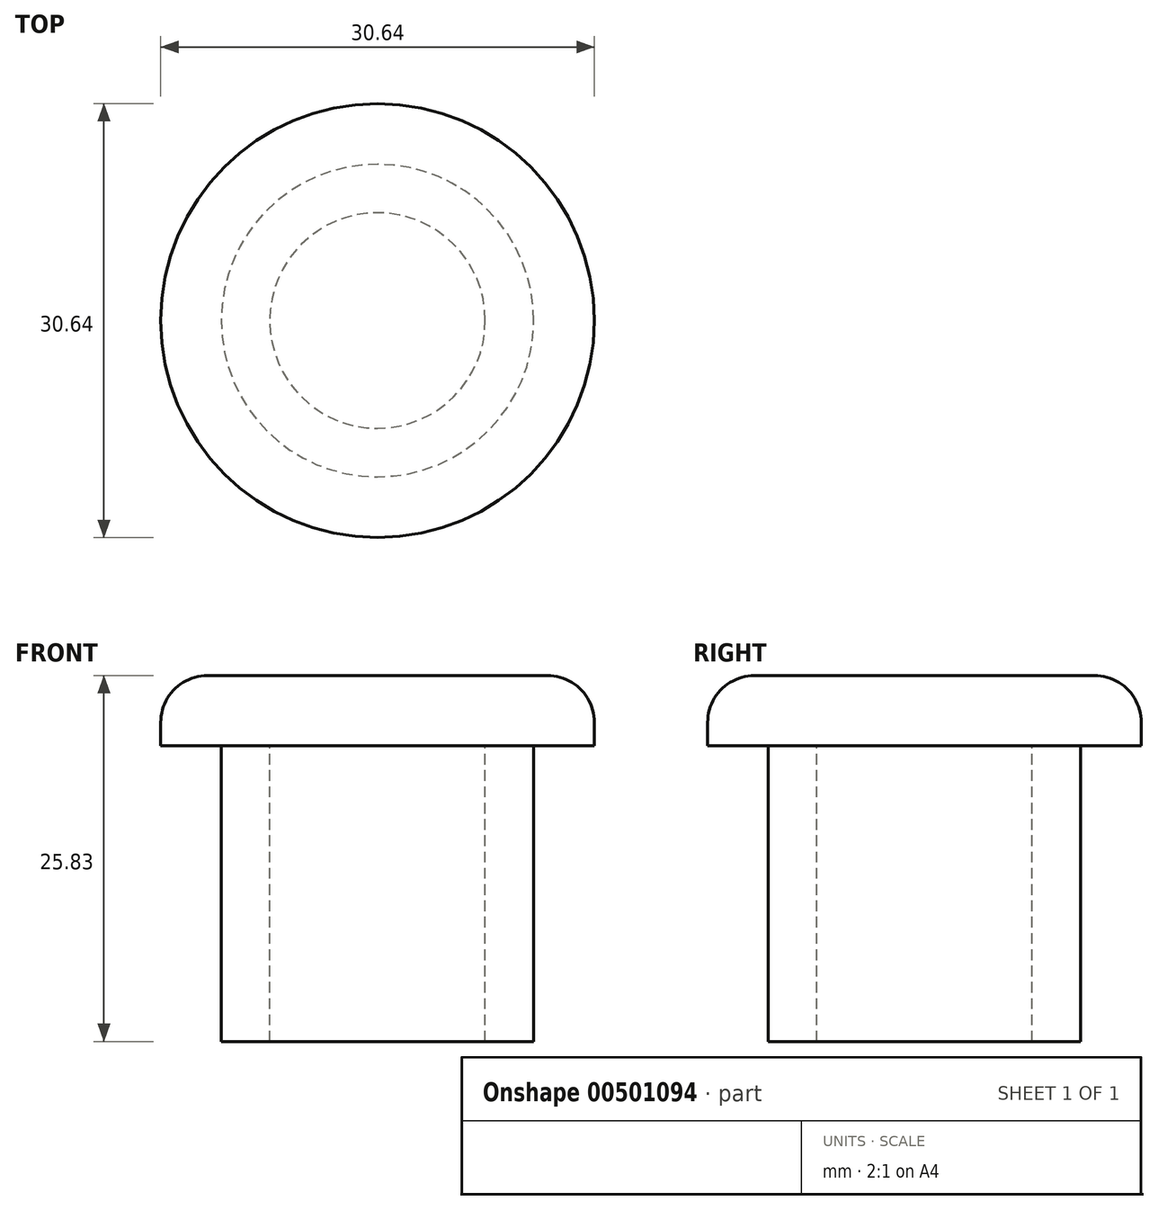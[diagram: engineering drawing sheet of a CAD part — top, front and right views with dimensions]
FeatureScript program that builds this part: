
annotation { "Feature Type Name" : "Feature", "Feature Type Description" : "" }
export const myFeature = defineFeature(function(context is Context, id is Id, definition is map)
    precondition{}
    {
        {
            var Q0;
            Q0=qCreatedBy(makeId("Front.planeOp"),FACE);
            var sketch = newSketch(context, id + "F0", { "sketchPlane" : qUnion([Q0])});
            skLineSegment(sketch, "E0", {"start": v(-11.03, 0) * mm, "end": v(-11.03, 20.87) * mm});
            skLineSegment(sketch, "E1", {"start": v(-11.03, 20.87) * mm, "end": v(-15.32, 20.87) * mm});
            skLineSegment(sketch, "E2", {"start": v(-15.32, 20.87) * mm, "end": v(-15.32, 22.53) * mm});
            skLineSegment(sketch, "E3", {"start": v(-12.01, 25.83) * mm, "end": v(0, 25.83) * mm});
            skLineSegment(sketch, "E4", {"start": v(0, 0) * mm, "end": v(-7.61, 0) * mm});
            skLineSegment(sketch, "E5", {"start": v(-7.61, 0) * mm, "end": v(-7.61, 20.87) * mm});
            skLineSegment(sketch, "E6", {"start": v(-7.61, 20.87) * mm, "end": v(0, 20.87) * mm});
            skLineSegment(sketch, "E7", {"start": v(0, 20.87) * mm, "end": v(0, 25.83) * mm});
            skLineSegment(sketch, "E8", {"start": v(-11.03, 0) * mm, "end": v(-7.61, 0) * mm});
            skPoint(sketch, "E9.visualSharp", {"position": v(-15.32, 25.83) * mm});
            skArc(sketch, "E9.filletArc", {"start": v(-12.01, 25.83) * mm, "mid": v(-14.35, 24.86) * mm, "end": v(-15.32, 22.53) * mm});
            skLineSegment(sketch, "E10", {"start": v(0, 20.87) * mm, "end": v(0, 0) * mm});
            skSolve(sketch);
        }
        {
            var Q0;
            Q0=makeQuery(id+"F0.imprint","IMPRINT",FACE,{"disambiguationData":[TD([[makeQuery(id+"F0.imprint","IMPRINT",EDGE,{"derivedFrom":sQuery(id+"F0.wireOp",EDGE,"E0")}),-1.0]])]});
            var Q1;
            Q1=sQuery(id+"F0.wireOp",EDGE,"E10");
            revolve(context, id + "F1", {"entities" : qUnion([Q0]), "axis" : qUnion([Q1]), "revolveType" : RevolveType.FULL});
        }
    });
